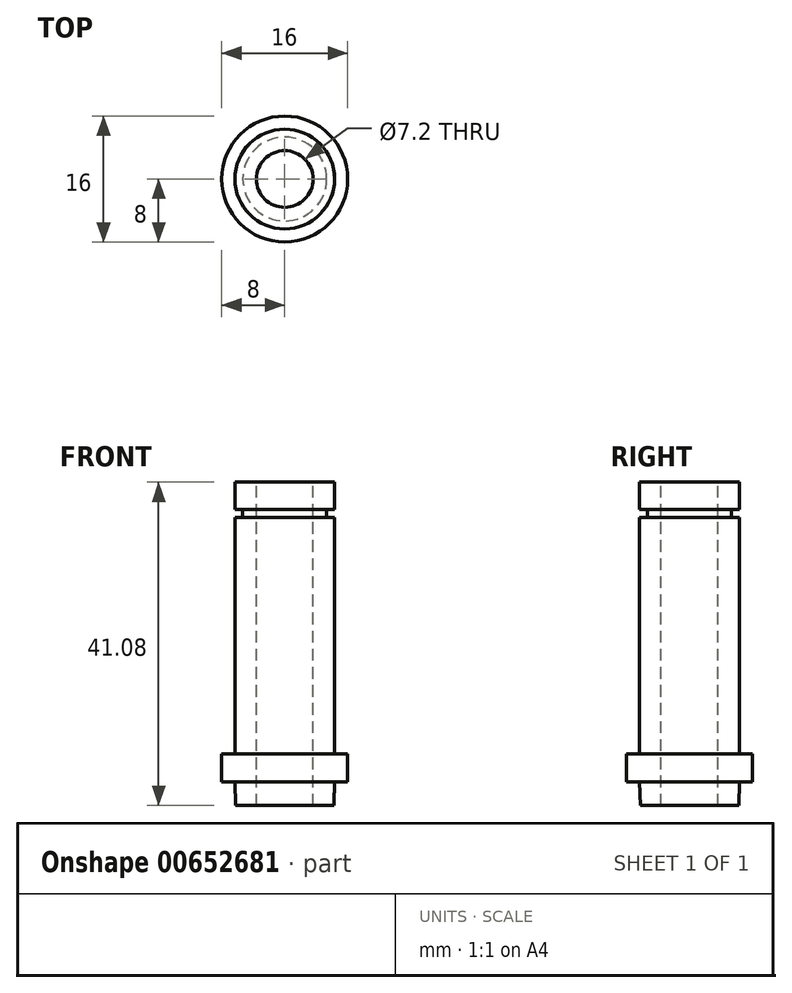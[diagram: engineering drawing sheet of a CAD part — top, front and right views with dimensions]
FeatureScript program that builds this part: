
annotation { "Feature Type Name" : "Feature", "Feature Type Description" : "" }
export const myFeature = defineFeature(function(context is Context, id is Id, definition is map)
    precondition{}
    {
        {
            var Q0;
            Q0=qCreatedBy(makeId("Right.planeOp"),FACE);
            var sketch = newSketch(context, id + "F0", { "sketchPlane" : qUnion([Q0])});
            skLineSegment(sketch, "E0", {"start": v(0, 3.48) * mm, "end": v(6.33, 3.48) * mm});
            skLineSegment(sketch, "E1", {"start": v(0, 3.48) * mm, "end": v(0, -37.6) * mm});
            skLineSegment(sketch, "E2", {"start": v(0, -37.6) * mm, "end": v(6.25, -37.6) * mm});
            skLineSegment(sketch, "E3", {"start": v(6.33, -34.62) * mm, "end": v(6.25, -37.6) * mm});
            skLineSegment(sketch, "E4", {"start": v(6.33, 3.48) * mm, "end": v(6.33, 0) * mm});
            skLineSegment(sketch, "E5", {"start": v(6.33, 0) * mm, "end": v(5.33, 0) * mm});
            skLineSegment(sketch, "E6", {"start": v(5.33, 0) * mm, "end": v(5.33, -1) * mm});
            skLineSegment(sketch, "E7", {"start": v(5.33, -1) * mm, "end": v(6.33, -1) * mm});
            skLineSegment(sketch, "E8", {"start": v(6.33, -1) * mm, "end": v(6.33, -31.02) * mm});
            skLineSegment(sketch, "E9", {"start": v(6.33, -31.02) * mm, "end": v(8, -31.02) * mm});
            skLineSegment(sketch, "E10", {"start": v(8, -31.02) * mm, "end": v(8, -34.62) * mm});
            skLineSegment(sketch, "E11", {"start": v(8, -34.62) * mm, "end": v(6.33, -34.62) * mm});
            skSolve(sketch);
        }
        {
            var Q0;
            Q0=qSketchRegion(id+"F0",true);
            var Q1;
            Q1=sQuery(id+"F0.wireOp",EDGE,"E1");
            revolve(context, id + "F1", {"entities" : qUnion([Q0]), "axis" : qUnion([Q1]), "revolveType" : RevolveType.FULL});
        }
        {
            var Q0;
            Q0=makeQuery(id+"F1.opRevolve","SWEPT_FACE",FACE,{"disambiguationData":[OSD([sQuery(id+"F0.wireOp",EDGE,"E0")])]});
            var sketch = newSketch(context, id + "F2", { "sketchPlane" : qUnion([Q0])});
            skCircle(sketch, "E12", {"center": v(0, 0) * mm, "radius": 3.6 * mm});
            skSolve(sketch);
        }
        {
            var Q0;
            Q0=qSketchRegion(id+"F2",true);
            extrude(context, id + "F3", {"entities" : qUnion([Q0]), "operationType" : NewBodyOperationType.REMOVE, "endBound" : BoundingType.THROUGH_ALL, "oppositeDirection" : true, "depth" : 25.4 * mm, "offsetDistance" : 25.4 * mm});
        }
    });
